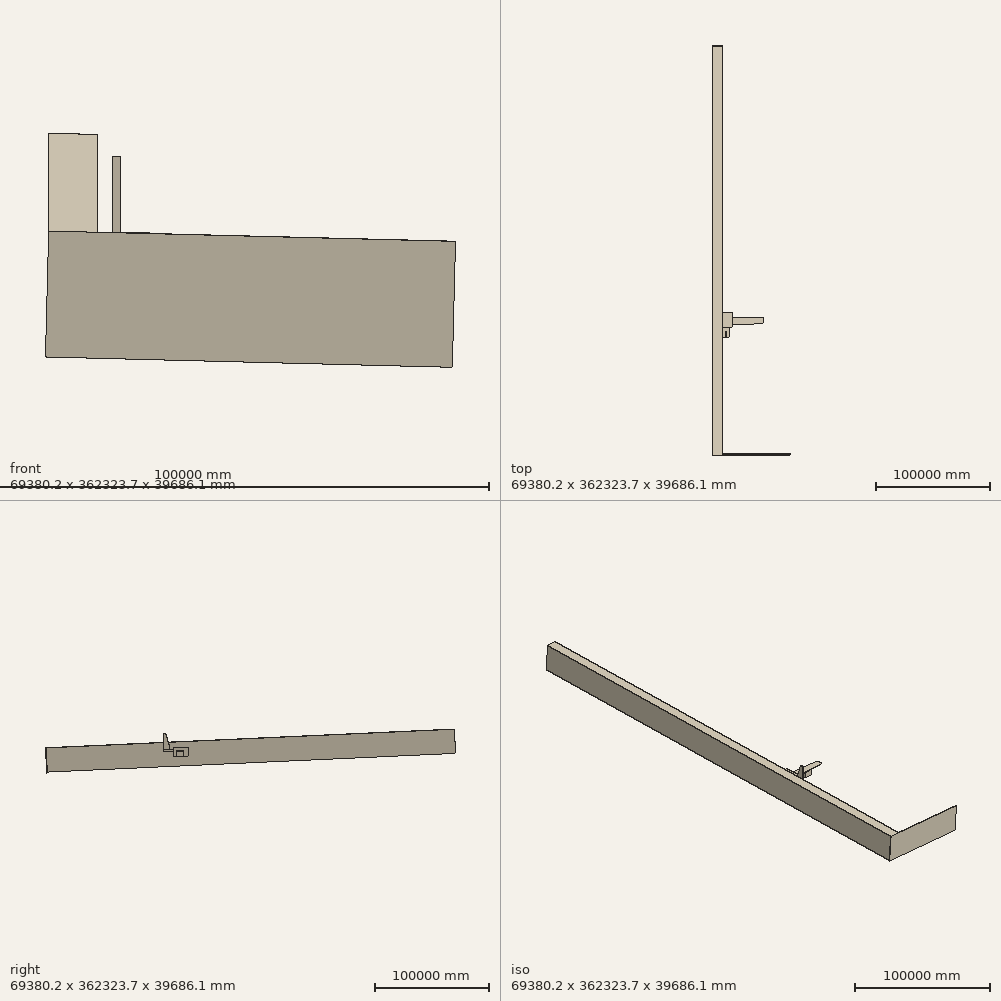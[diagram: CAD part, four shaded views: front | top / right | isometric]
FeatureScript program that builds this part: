
annotation { "Feature Type Name" : "Feature", "Feature Type Description" : "" }
export const myFeature = defineFeature(function(context is Context, id is Id, definition is map)
    precondition{}
    {
        {
            var Q0;
            Q0=qCreatedBy(makeId("Top.planeOp"),FACE);
            var sketch = newSketch(context, id + "F0", { "sketchPlane" : qUnion([Q0])});
            skCircle(sketch, "E0.cCircle", {"center": v(-54.96, 41.99) * mm, "radius": 97.74 * mm, "construction": true});
            skLineSegment(sketch, "E0.0", {"start": v(54.6, -8.93) * mm, "end": v(-69.52, -77.95) * mm});
            skLineSegment(sketch, "E0.1", {"start": v(-69.52, -77.95) * mm, "end": v(-173.53, 18.78) * mm});
            skLineSegment(sketch, "E0.2", {"start": v(-173.53, 18.78) * mm, "end": v(-113.67, 147.58) * mm});
            skLineSegment(sketch, "E0.3", {"start": v(-113.67, 147.58) * mm, "end": v(27.32, 130.46) * mm});
            skLineSegment(sketch, "E0.4", {"start": v(27.32, 130.46) * mm, "end": v(54.6, -8.93) * mm});
            skPoint(sketch, "E0.0.midPoint", {"position": v(-7.46, -43.44) * mm});
            skSolve(sketch);
        }
        {
            var Q0;
            Q0=makeQuery(id+"F0.imprint","IMPRINT",FACE,{"disambiguationData":[TD([[makeQuery(id+"F0.imprint","IMPRINT",EDGE,{"derivedFrom":sQuery(id+"F0.wireOp",EDGE,"E0.0")}),-1.0]])]});
            extrude(context, id + "F1", {"entities" : qUnion([Q0]), "depth" : 119.13 * mm, "offsetDistance" : 25.4 * mm});
        }
        {
            var Q0;
            Q0=makeQuery(id+"F1.opExtrude","CAP_FACE",FACE,{"disambiguationData":[OSD([sQuery(id+"F0.wireOp",EDGE,"E0.0"),sQuery(id+"F0.wireOp",EDGE,"E0.1"),sQuery(id+"F0.wireOp",EDGE,"E0.2"),sQuery(id+"F0.wireOp",EDGE,"E0.3"),sQuery(id+"F0.wireOp",EDGE,"E0.4")])],"isStart":false});
            var sketch = newSketch(context, id + "F2", { "sketchPlane" : qUnion([Q0])});
            skCircle(sketch, "E1", {"center": v(-77.6, 64.7) * mm, "radius": 56.6 * mm});
            skSolve(sketch);
        }
        {
            var Q0;
            Q0=makeQuery(id+"F2.imprint","IMPRINT",FACE,{"disambiguationData":[TD([[makeQuery(id+"F2.imprint","IMPRINT",EDGE,{"derivedFrom":sQuery(id+"F2.wireOp",EDGE,"E1")}),1.0]])]});
            extrude(context, id + "F3", {"entities" : qUnion([Q0]), "operationType" : NewBodyOperationType.ADD, "depth" : 538.48 * mm, "offsetDistance" : 25.4 * mm});
        }
        {
            var Q0;
            Q0=makeQuery(id+"F1.opExtrude","SWEPT_FACE",FACE,{"disambiguationData":[OSD([sQuery(id+"F0.wireOp",EDGE,"E0.0")])]});
            var sketch = newSketch(context, id + "F4", { "sketchPlane" : qUnion([Q0])});
            skLineSegment(sketch, "E2.bottom", {"start": v(-98.64, 119.13) * mm, "end": v(43.39, 119.13) * mm});
            skLineSegment(sketch, "E2.top", {"start": v(-98.64, 0) * mm, "end": v(43.39, 0) * mm});
            skLineSegment(sketch, "E2.left", {"start": v(-98.64, 119.13) * mm, "end": v(-98.64, 0) * mm});
            skLineSegment(sketch, "E2.right", {"start": v(43.39, 119.13) * mm, "end": v(43.39, 0) * mm});
            skSolve(sketch);
        }
        {
            var Q0;
            Q0=makeQuery(id+"F4.imprint","IMPRINT",FACE,{"disambiguationData":[TD([[makeQuery(id+"F4.imprint","IMPRINT",EDGE,{"derivedFrom":sQuery(id+"F4.wireOp",EDGE,"E2.bottom")}),1.0]])]});
            extrude(context, id + "F5", {"entities" : qUnion([Q0]), "operationType" : NewBodyOperationType.ADD, "depth" : 1600.2 * mm, "offsetDistance" : 25.4 * mm, "hasDraft" : true, "draftAngle" : 3 * degree, "draftPullDirection" : true});
        }
        {
            var Q0;
            Q0=makeQuery(id+"F5.opExtrude","SWEPT_FACE",FACE,{"disambiguationData":[OSD([sQuery(id+"F4.wireOp",EDGE,"E2.bottom")])]});
            var sketch = newSketch(context, id + "F6", { "sketchPlane" : qUnion([Q0])});
            skLineSegment(sketch, "E3.bottom", {"start": v(330.61, -716.76) * mm, "end": v(0, -716.76) * mm});
            skLineSegment(sketch, "E3.top", {"start": v(330.61, -118.56) * mm, "end": v(0, -118.56) * mm});
            skLineSegment(sketch, "E3.left", {"start": v(330.61, -716.76) * mm, "end": v(330.61, -118.56) * mm});
            skLineSegment(sketch, "E3.right", {"start": v(0, -716.76) * mm, "end": v(0, -118.56) * mm});
            skSolve(sketch);
        }
        {
            var Q0;
            {var subQ0=sQuery(id+"F6.wireOp",EDGE,"E3.bottom");Q0=makeQuery(id+"F6.imprint","IMPRINT",FACE,{"disambiguationData":[TD([[makeQuery(id+"F6.imprint","IMPRINT",EDGE,{"derivedFrom":subQ0}),-1.0]])]});}
            var Q1;
            {var subQ0=sQuery(id+"F6.wireOp",EDGE,"E3.left");var subQ1=sQuery(id+"F6.wireOp",EDGE,"E3.top");var subQ2=makeQuery(id+"F6.imprint","INTERSECT",VERTEX,{"derivedFrom":[subQ1,subQ0]});Q1=makeQuery(id+"F6.imprint","IMPRINT",FACE,{"disambiguationData":[TD([[makeQuery(id+"F6.imprint","IMPRINT",EDGE,{"disambiguationData":[TD([[subQ2,-1.0]])],"derivedFrom":subQ1}),1.0]])]});}
            extrude(context, id + "F7", {"entities" : qUnion([Q0, Q1]), "depth" : 21336 * mm, "offsetDistance" : 25.4 * mm});
        }
        {
            var Q0;
            Q0=makeQuery(id+"F7.opExtrude","SWEPT_FACE",FACE,{"disambiguationData":[OSD([sQuery(id+"F6.wireOp",EDGE,"E3.right")])]});
            extrude(context, id + "F8", {"entities" : qUnion([Q0]), "operationType" : NewBodyOperationType.ADD, "depth" : 68529.2 * mm, "offsetDistance" : 25.4 * mm});
        }
        {
            var Q0;
            Q0=makeQuery(id+"F8.opExtrude","SWEPT_FACE",FACE,{"disambiguationData":[OSD([sQuery(id+"F4.wireOp",EDGE,"E2.bottom"),sQuery(id+"F4.wireOp",EDGE,"E2.left"),sQuery(id+"F6.wireOp",EDGE,"E3.right")])]});
            var sketch = newSketch(context, id + "F9", { "sketchPlane" : qUnion([Q0])});
            skLineSegment(sketch, "E4.bottom", {"start": v(67961.3, 23192.77) * mm, "end": v(59651.59, 23192.77) * mm});
            skLineSegment(sketch, "E4.top", {"start": v(67961.3, 1638.45) * mm, "end": v(59651.59, 1638.45) * mm});
            skLineSegment(sketch, "E4.left", {"start": v(67961.3, 23192.77) * mm, "end": v(67961.3, 1638.45) * mm});
            skLineSegment(sketch, "E4.right", {"start": v(59651.59, 23192.77) * mm, "end": v(59651.59, 1638.45) * mm});
            skSolve(sketch);
        }
        {
            var Q0;
            {var subQ1=sQuery(id+"F6.wireOp",EDGE,"E3.right");var subQ2=sQuery(id+"F4.wireOp",EDGE,"E2.left");var subQ3=sQuery(id+"F4.wireOp",EDGE,"E2.bottom");var subQ4=makeQuery(id+"F8.opExtrude","SWEPT_EDGE",EDGE,{"disambiguationData":[OSD([subQ3,subQ2,subQ1]),TDD([makeQuery(id+"F7.opExtrude","CAP_VERTEX",VERTEX,{"disambiguationData":[OSD([subQ3,subQ2,subQ1])],"isStart":false})])]});var subQ8=sQuery(id+"F9.wireOp",EDGE,"E4.right");var subQ9=makeQuery(id+"F9.imprint","INTERSECT",VERTEX,{"derivedFrom":[subQ4,subQ8]});Q0=makeQuery(id+"F9.imprint","IMPRINT",FACE,{"disambiguationData":[TD([[makeQuery(id+"F9.imprint","IMPRINT",EDGE,{"disambiguationData":[TD([[subQ9,-1.0]])],"derivedFrom":subQ8}),1.0]])]});}
            extrude(context, id + "F10", {"entities" : qUnion([Q0]), "operationType" : NewBodyOperationType.ADD, "depth" : 361188 * mm, "offsetDistance" : 25.4 * mm});
        }
        {
            var Q0;
            Q0=makeQuery(id+"F10.opExtrude","SWEPT_FACE",FACE,{"disambiguationData":[OSD([sQuery(id+"F9.wireOp",EDGE,"E4.right")])]});
            var sketch = newSketch(context, id + "F11", { "sketchPlane" : qUnion([Q0])});
            skLineSegment(sketch, "E5.bottom", {"start": v(110919.96, 22936.45) * mm, "end": v(124729.1, 22936.45) * mm});
            skLineSegment(sketch, "E5.top", {"start": v(110919.96, 15767.88) * mm, "end": v(124729.1, 15767.88) * mm});
            skLineSegment(sketch, "E5.left", {"start": v(110919.96, 22936.45) * mm, "end": v(110919.96, 15767.88) * mm});
            skLineSegment(sketch, "E5.right", {"start": v(124729.1, 22936.45) * mm, "end": v(124729.1, 15767.88) * mm});
            skSolve(sketch);
        }
        {
            var Q0;
            Q0=makeQuery(id+"F11.imprint","IMPRINT",FACE,{"disambiguationData":[TD([[makeQuery(id+"F11.imprint","IMPRINT",EDGE,{"derivedFrom":sQuery(id+"F11.wireOp",EDGE,"E5.bottom")}),-1.0]])]});
            extrude(context, id + "F12", {"entities" : qUnion([Q0]), "operationType" : NewBodyOperationType.ADD, "depth" : 8661.4 * mm, "offsetDistance" : 25.4 * mm});
        }
        {
            var Q0;
            Q0=makeQuery(id+"F12.opExtrude","CAP_FACE",FACE,{"disambiguationData":[OSD([sQuery(id+"F11.wireOp",EDGE,"E5.bottom"),sQuery(id+"F11.wireOp",EDGE,"E5.top"),sQuery(id+"F11.wireOp",EDGE,"E5.left"),sQuery(id+"F11.wireOp",EDGE,"E5.right")])],"isStart":false});
            var sketch = newSketch(context, id + "F13", { "sketchPlane" : qUnion([Q0])});
            skLineSegment(sketch, "E6.bottom", {"start": v(114093.42, 20640.26) * mm, "end": v(120607.84, 20640.26) * mm});
            skLineSegment(sketch, "E6.top", {"start": v(114093.42, 19681.53) * mm, "end": v(120607.84, 19681.53) * mm});
            skLineSegment(sketch, "E6.left", {"start": v(114093.42, 20640.26) * mm, "end": v(114093.42, 19681.53) * mm});
            skLineSegment(sketch, "E6.right", {"start": v(120607.84, 20640.26) * mm, "end": v(120607.84, 19681.53) * mm});
            skSolve(sketch);
        }
        {
            var Q0;
            Q0=makeQuery(id+"F13.imprint","IMPRINT",FACE,{"disambiguationData":[TD([[makeQuery(id+"F13.imprint","IMPRINT",EDGE,{"derivedFrom":sQuery(id+"F13.wireOp",EDGE,"E6.bottom")}),-1.0]])]});
            extrude(context, id + "F14", {"entities" : qUnion([Q0]), "operationType" : NewBodyOperationType.ADD, "depth" : 31750 * mm, "offsetDistance" : 25.4 * mm, "hasDraft" : true, "draftAngle" : 1 * degree, "draftPullDirection" : true});
        }
        {
            var Q0;
            Q0=makeQuery(id+"F14.opExtrude","SWEPT_FACE",FACE,{"disambiguationData":[OSD([sQuery(id+"F13.wireOp",EDGE,"E6.top")])]});
            var sketch = newSketch(context, id + "F15", { "sketchPlane" : qUnion([Q0])});
            skLineSegment(sketch, "E7.bottom", {"start": v(-41214.15, -114257.9) * mm, "end": v(-35510.1, -114257.9) * mm});
            skLineSegment(sketch, "E7.top", {"start": v(-41214.15, -120343.8) * mm, "end": v(-35510.1, -120343.8) * mm});
            skLineSegment(sketch, "E7.left", {"start": v(-41214.15, -114257.9) * mm, "end": v(-41214.15, -120343.8) * mm});
            skLineSegment(sketch, "E7.right", {"start": v(-35510.1, -114257.9) * mm, "end": v(-35510.1, -120343.8) * mm});
            skSolve(sketch);
        }
        {
            var Q0;
            {var subQ0=sQuery(id+"F15.wireOp",EDGE,"E7.top");Q0=makeQuery(id+"F15.imprint","IMPRINT",FACE,{"disambiguationData":[TD([[makeQuery(id+"F15.imprint","IMPRINT",EDGE,{"derivedFrom":subQ0}),1.0]])]});}
            extrude(context, id + "F16", {"entities" : qUnion([Q0]), "operationType" : NewBodyOperationType.ADD, "depth" : 4572 * mm, "offsetDistance" : 25.4 * mm});
        }
        {
            var Q0;
            Q0=makeQuery(id+"F16.opExtrude","SWEPT_FACE",FACE,{"disambiguationData":[OSD([sQuery(id+"F13.wireOp",EDGE,"E6.top"),sQuery(id+"F13.wireOp",EDGE,"E6.left")])]});
            var sketch = newSketch(context, id + "F17", { "sketchPlane" : qUnion([Q0])});
            skCircle(sketch, "E8", {"center": v(-37596.61, 17595.17) * mm, "radius": 1717.47 * mm});
            skPoint(sketch, "E8.centerSnap0", {"position": v(-39527.25, 17595.17) * mm});
            skSolve(sketch);
        }
        {
            var Q0;
            Q0=sQuery(id+"F17.wireOp",EDGE,"E8");
            extrude(context, id + "F18", {"bodyType" : ToolBodyType.SURFACE, "surfaceEntities" : qUnion([Q0]), "depth" : 4064 * mm, "offsetDistance" : 25.4 * mm});
        }
        {
            var Q0;
            Q0=makeQuery(id+"F12.opExtrude","SWEPT_FACE",FACE,{"disambiguationData":[OSD([sQuery(id+"F11.wireOp",EDGE,"E5.right")])]});
            var sketch = newSketch(context, id + "F19", { "sketchPlane" : qUnion([Q0])});
            skLineSegment(sketch, "E9.bottom", {"start": v(52910.36, 21575.83) * mm, "end": v(59651.59, 21575.83) * mm});
            skLineSegment(sketch, "E9.top", {"start": v(52910.36, 20264.8) * mm, "end": v(59651.59, 20264.8) * mm});
            skLineSegment(sketch, "E9.left", {"start": v(52910.36, 21575.83) * mm, "end": v(52910.36, 20264.8) * mm});
            skLineSegment(sketch, "E9.right", {"start": v(59651.59, 21575.83) * mm, "end": v(59651.59, 20264.8) * mm});
            skSolve(sketch);
        }
        {
            var Q0;
            Q0=makeQuery(id+"F19.imprint","IMPRINT",FACE,{"disambiguationData":[TD([[makeQuery(id+"F19.imprint","IMPRINT",EDGE,{"derivedFrom":sQuery(id+"F19.wireOp",EDGE,"E9.bottom")}),-1.0]])]});
            extrude(context, id + "F20", {"entities" : qUnion([Q0]), "operationType" : NewBodyOperationType.ADD, "oppositeDirection" : true, "depth" : 22098 * mm, "offsetDistance" : 25.4 * mm});
        }
        {
            var Q0;
            Q0=makeQuery(id+"F20.opExtrude","SWEPT_FACE",FACE,{"disambiguationData":[OSD([sQuery(id+"F19.wireOp",EDGE,"E9.bottom")])]});
            var sketch = newSketch(context, id + "F21", { "sketchPlane" : qUnion([Q0])});
            skLineSegment(sketch, "E10.bottom", {"start": v(-55831.32, 107516.23) * mm, "end": v(-57096.53, 107516.23) * mm});
            skLineSegment(sketch, "E10.top", {"start": v(-55831.32, 102631.1) * mm, "end": v(-57096.53, 102631.1) * mm});
            skLineSegment(sketch, "E10.left", {"start": v(-55831.32, 107516.23) * mm, "end": v(-55831.32, 102631.1) * mm});
            skLineSegment(sketch, "E10.right", {"start": v(-57096.53, 107516.23) * mm, "end": v(-57096.53, 102631.1) * mm});
            skSolve(sketch);
        }
        {
            var Q0;
            Q0=makeQuery(id+"F21.imprint","IMPRINT",FACE,{"disambiguationData":[TD([[makeQuery(id+"F21.imprint","IMPRINT",EDGE,{"derivedFrom":sQuery(id+"F21.wireOp",EDGE,"E10.bottom")}),1.0]])]});
            extrude(context, id + "F22", {"entities" : qUnion([Q0]), "operationType" : NewBodyOperationType.ADD, "depth" : 14224 * mm, "offsetDistance" : 25.4 * mm});
        }
        {
            var Q0;
            Q0=makeQuery(id+"F22.opExtrude","SWEPT_FACE",FACE,{"disambiguationData":[OSD([sQuery(id+"F21.wireOp",EDGE,"E10.left")])]});
            var sketch = newSketch(context, id + "F23", { "sketchPlane" : qUnion([Q0])});
            skLineSegment(sketch, "E11", {"start": v(104515.12, 35799.83) * mm, "end": v(107516.23, 25550.56) * mm});
            skLineSegment(sketch, "E12", {"start": v(107516.23, 25550.56) * mm, "end": v(112072.41, 35799.83) * mm});
            skLineSegment(sketch, "E13", {"start": v(112072.41, 35799.83) * mm, "end": v(104515.12, 35799.83) * mm});
            skSolve(sketch);
        }
        {
            var Q0;
            {var subQ0=sQuery(id+"F23.wireOp",EDGE,"E11");Q0=makeQuery(id+"F23.imprint","IMPRINT",FACE,{"disambiguationData":[TD([[makeQuery(id+"F23.imprint","IMPRINT",EDGE,{"derivedFrom":subQ0}),1.0]])]});}
            extrude(context, id + "F24", {"entities" : qUnion([Q0]), "operationType" : NewBodyOperationType.REMOVE, "oppositeDirection" : true, "depth" : 2082.8 * mm, "offsetDistance" : 25.4 * mm});
        }
    });
